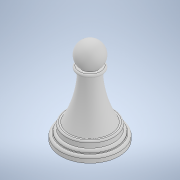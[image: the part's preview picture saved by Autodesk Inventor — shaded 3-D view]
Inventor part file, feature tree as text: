
AUTODESK INVENTOR PART (.ipt)
format: ipt  version: 2022 (Build 260153000, 153)  size: 208,896 bytes
history: native  units: mm
features: other x3, fillet x2, revolve x1, sketch x1, projected_geometry x1
ambient origin geometry x8: Origin, YZ Plane, XZ Plane, XY Plane, X Axis, Y Axis, Z Axis, Center Point
bodies: Solid1 (feature_tree)
feature tree (8):
  other  "Chess Piece Base.ipt"
  revolve  "Revolution1"  [1 undecoded]
  fillet  "Fillet1"  Radius=2.0mm
  fillet  "Fillet2"  Radius=3.0mm
  other  "Solid1::Chess Piece Base.ipt"
  other  "TaggingFeature1"
  sketch  "Sketch1"  dims[d0=10.0mm d1=25.0mm d2=2.0mm d3=3.0mm d4=8.0mm d6=4.0mm d8=90.0deg d10=1.0mm d11=1.0mm d12=1.0mm d13=0.5mm d14=0.5mm]
  projected_geometry  "Projected Loop1"
note: 1 required parameter value undecoded (feature->parameter linkage not recoverable at this tier; creation-order binding heuristic only, values carry confidence <= 0.55)
